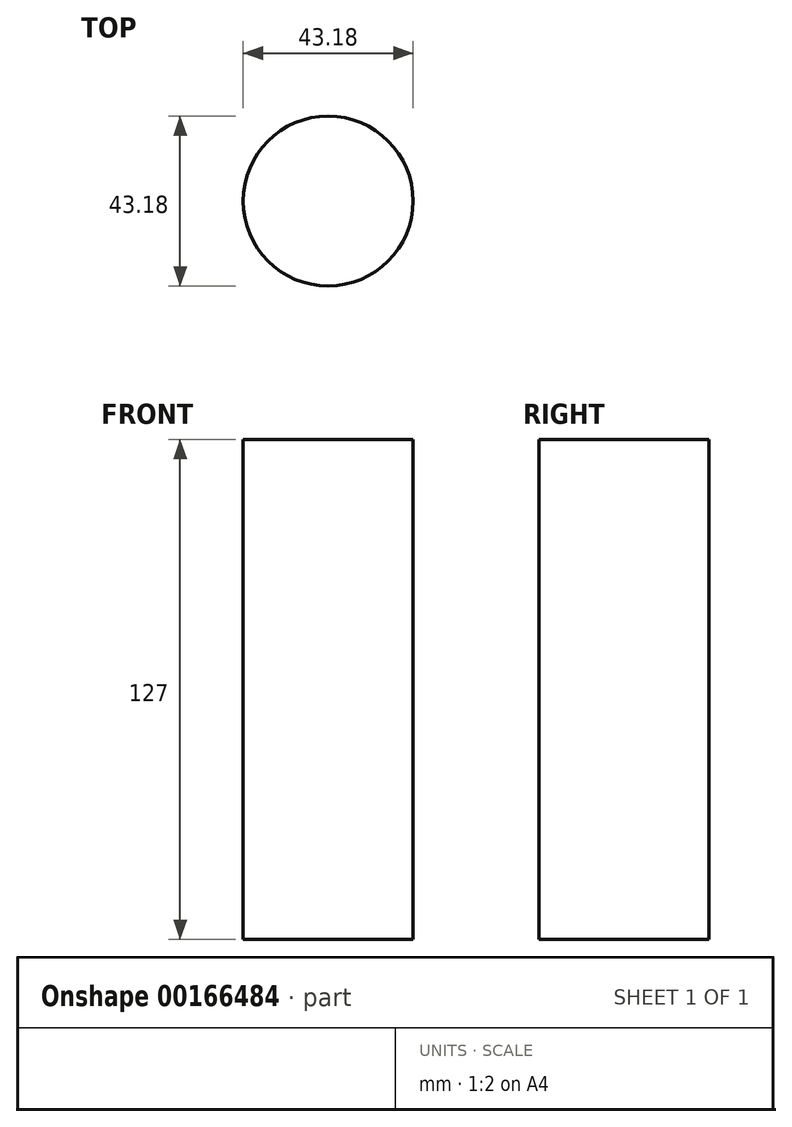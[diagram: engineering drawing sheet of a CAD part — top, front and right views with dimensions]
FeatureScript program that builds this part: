
annotation { "Feature Type Name" : "Feature", "Feature Type Description" : "" }
export const myFeature = defineFeature(function(context is Context, id is Id, definition is map)
    precondition{}
    {
        {
            var Q0;
            Q0=qCreatedBy(makeId("Top.planeOp"),FACE);
            var sketch = newSketch(context, id + "F0", { "sketchPlane" : qUnion([Q0])});
            skCircle(sketch, "E0", {"center": v(0, 0) * mm, "radius": 21.59 * mm});
            skSolve(sketch);
        }
        {
            var Q0;
            Q0 = qSketchRegion(id + "F0", true);
            extrude(context, id + "F1", {"entities" : qUnion([Q0]), "depth" : 127 * mm});
        }
    });
